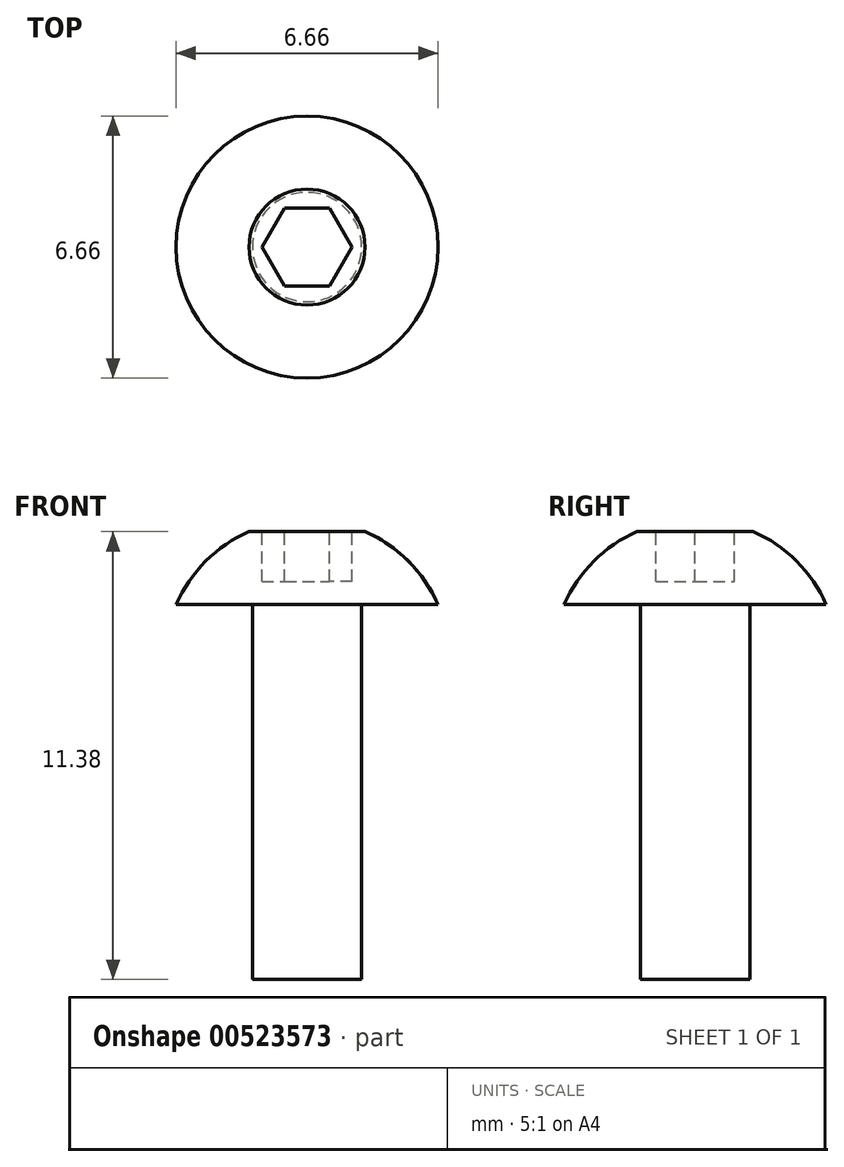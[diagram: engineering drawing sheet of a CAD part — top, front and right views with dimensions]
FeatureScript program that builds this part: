
annotation { "Feature Type Name" : "Feature", "Feature Type Description" : "" }
export const myFeature = defineFeature(function(context is Context, id is Id, definition is map)
    precondition{}
    {
        {
            var Q0;
            Q0=qCreatedBy(makeId("Front.planeOp"),FACE);
            var sketch = newSketch(context, id + "F0", { "sketchPlane" : qUnion([Q0])});
            skLineSegment(sketch, "E0", {"start": v(1.39, 0) * mm, "end": v(3.33, 0) * mm});
            skLineSegment(sketch, "E1", {"start": v(0, 0) * mm, "end": v(0, 1.85) * mm});
            skLineSegment(sketch, "E2", {"start": v(0, 1.85) * mm, "end": v(1.47, 1.85) * mm});
            skArc(sketch, "E3", {"start": v(3.33, 0) * mm, "mid": v(2.57, 1.1) * mm, "end": v(1.47, 1.85) * mm});
            skLineSegment(sketch, "E4", {"start": v(0, 0) * mm, "end": v(0, -9.53) * mm});
            skLineSegment(sketch, "E5", {"start": v(0, -9.53) * mm, "end": v(1.39, -9.53) * mm});
            skLineSegment(sketch, "E6", {"start": v(1.39, -9.53) * mm, "end": v(1.39, 0) * mm});
            skSolve(sketch);
        }
        {
            var Q0;
            Q0=makeQuery(id+"F0.imprint","IMPRINT",FACE,{"disambiguationData":[TD([[makeQuery(id+"F0.imprint","IMPRINT",EDGE,{"derivedFrom":sQuery(id+"F0.wireOp",EDGE,"E0")}),1.0]])]});
            var Q1;
            Q1=sQuery(id+"F0.wireOp",EDGE,"E4");
            revolve(context, id + "F1", {"entities" : qUnion([Q0]), "axis" : qUnion([Q1]), "revolveType" : RevolveType.FULL});
        }
        {
            var Q0;
            Q0=makeQuery(id+"F1.opRevolve","SWEPT_FACE",FACE,{"disambiguationData":[OSD([sQuery(id+"F0.wireOp",EDGE,"E2")])]});
            var sketch = newSketch(context, id + "F2", { "sketchPlane" : qUnion([Q0])});
            skCircle(sketch, "E7.0.0", {"center": v(0, 0) * mm, "radius": 1.47 * mm});
            skCircle(sketch, "E8.cCircle", {"center": v(0, 0) * mm, "radius": 1 * mm, "construction": true});
            skLineSegment(sketch, "E8.0", {"start": v(-0.57, 1) * mm, "end": v(0.57, 1) * mm});
            skLineSegment(sketch, "E8.1", {"start": v(0.57, 1) * mm, "end": v(1.15, 0) * mm});
            skLineSegment(sketch, "E8.2", {"start": v(1.15, 0) * mm, "end": v(0.57, -1) * mm});
            skLineSegment(sketch, "E8.3", {"start": v(0.57, -1) * mm, "end": v(-0.57, -1) * mm});
            skLineSegment(sketch, "E8.4", {"start": v(-0.57, -1) * mm, "end": v(-1.15, 0) * mm});
            skLineSegment(sketch, "E8.5", {"start": v(-1.15, 0) * mm, "end": v(-0.57, 1) * mm});
            skPoint(sketch, "E8.0.midPoint", {"position": v(0, 1) * mm});
            skSolve(sketch);
        }
        {
            var Q0;
            Q0=makeQuery(id+"F2.imprint","IMPRINT",FACE,{"disambiguationData":[TD([[makeQuery(id+"F2.imprint","IMPRINT",EDGE,{"derivedFrom":sQuery(id+"F2.wireOp",EDGE,"E8.0")}),-1.0]])]});
            extrude(context, id + "F3", {"entities" : qUnion([Q0]), "operationType" : NewBodyOperationType.REMOVE, "oppositeDirection" : true, "depth" : 1.27 * mm, "offsetDistance" : 25.4 * mm});
        }
    });
